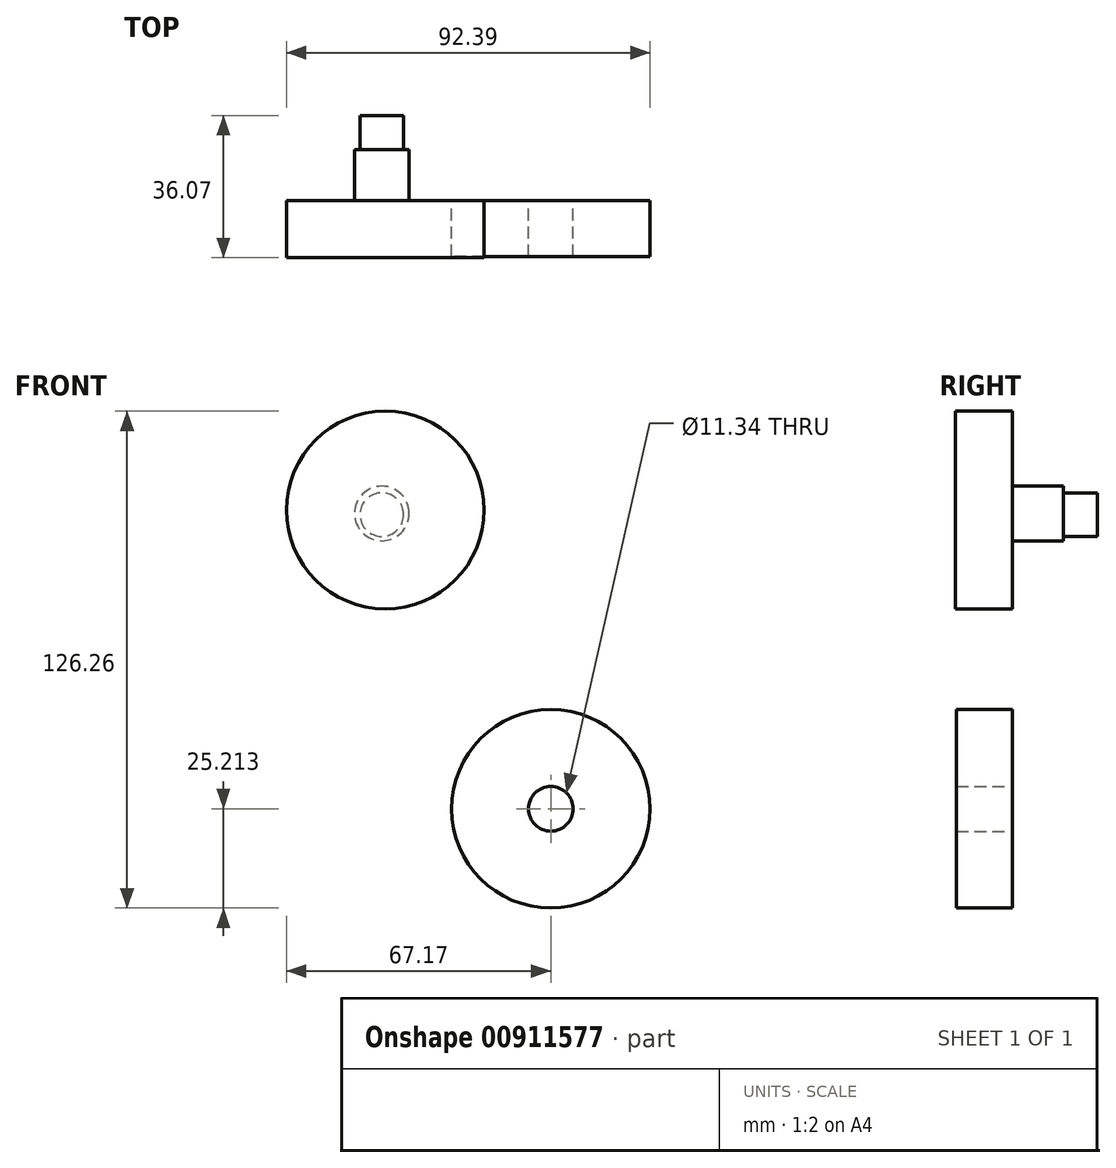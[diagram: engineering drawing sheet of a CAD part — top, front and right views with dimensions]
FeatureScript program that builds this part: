
annotation { "Feature Type Name" : "Feature", "Feature Type Description" : "" }
export const myFeature = defineFeature(function(context is Context, id is Id, definition is map)
    precondition{}
    {
        {
            var Q0;
            Q0=qCreatedBy(makeId("Front.planeOp"),FACE);
            var sketch = newSketch(context, id + "F0", { "sketchPlane" : qUnion([Q0])});
            skCircle(sketch, "E0", {"center": v(-35.48, 29.05) * mm, "radius": 25.12 * mm});
            skSolve(sketch);
        }
        {
            var Q0;
            Q0=makeQuery(id+"F0.imprint","IMPRINT",FACE,{"disambiguationData":[TD([[makeQuery(id+"F0.imprint","IMPRINT",EDGE,{"derivedFrom":sQuery(id+"F0.wireOp",EDGE,"E0")}),1.0]])]});
            extrude(context, id + "F1", {"entities" : qUnion([Q0]), "depth" : 14.48 * mm, "offsetDistance" : 25.4 * mm});
        }
        {
            var Q0;
            Q0=qCreatedBy(makeId("Front.planeOp"),FACE);
            var sketch = newSketch(context, id + "F2", { "sketchPlane" : qUnion([Q0])});
            skCircle(sketch, "E1", {"center": v(-36.35, 27.89) * mm, "radius": 5.54 * mm});
            skSolve(sketch);
        }
        {
            var Q0;
            Q0 = qSketchRegion(id + "F2", true);
            extrude(context, id + "F3", {"entities" : qUnion([Q0]), "operationType" : NewBodyOperationType.ADD, "oppositeDirection" : true, "depth" : 17.27 * mm, "offsetDistance" : 25.4 * mm});
        }
        {
            var Q0;
            Q0=qCreatedBy(makeId("Front.planeOp"),FACE);
            var sketch = newSketch(context, id + "F4", { "sketchPlane" : qUnion([Q0])});
            skCircle(sketch, "E2", {"center": v(6.57, -46.87) * mm, "radius": 25.22 * mm});
            skCircle(sketch, "E3", {"center": v(6.57, -46.87) * mm, "radius": 5.67 * mm});
            skSolve(sketch);
        }
        {
            var Q0;
            Q0 = qSketchRegion(id + "F4", true);
            extrude(context, id + "F5", {"entities" : qUnion([Q0]), "depth" : 14.22 * mm, "offsetDistance" : 25.4 * mm});
        }
        {
            var Q0;
            Q0=qCreatedBy(makeId("Front.planeOp"),FACE);
            var sketch = newSketch(context, id + "F6", { "sketchPlane" : qUnion([Q0])});
            skCircle(sketch, "E4", {"center": v(-36.35, 28.18) * mm, "radius": 6.94 * mm});
            skCircle(sketch, "E5", {"center": v(-36.35, 28.18) * mm, "radius": 3.8 * mm});
            skSolve(sketch);
        }
        {
            var Q0;
            Q0 = qSketchRegion(id + "F6", true);
            extrude(context, id + "F7", {"entities" : qUnion([Q0]), "operationType" : NewBodyOperationType.ADD, "oppositeDirection" : true, "depth" : 12.95 * mm, "offsetDistance" : 25.4 * mm});
        }
        {
            var Q0;
            Q0=qCreatedBy(makeId("Front.planeOp"),FACE);
            var sketch = newSketch(context, id + "F8", { "sketchPlane" : qUnion([Q0])});
            skCircle(sketch, "E6", {"center": v(-36.35, 27.3) * mm, "radius": 3.66 * mm});
            skCircle(sketch, "E7", {"center": v(-36.35, 27.3) * mm, "radius": 2.35 * mm});
            skSolve(sketch);
        }
        {
            var Q0;
            Q0 = qSketchRegion(id + "F8", true);
            var Q1;
            Q1=makeQuery(id+"F3.opExtrude","CAP_FACE",FACE,{"disambiguationData":[OSD([sQuery(id+"F2.wireOp",EDGE,"E1")])],"isStart":false});
            extrude(context, id + "F9", {"entities" : qUnion([Q0, Q1]), "operationType" : NewBodyOperationType.ADD, "oppositeDirection" : true, "depth" : 4.32 * mm, "offsetDistance" : 25.4 * mm});
        }
    });
